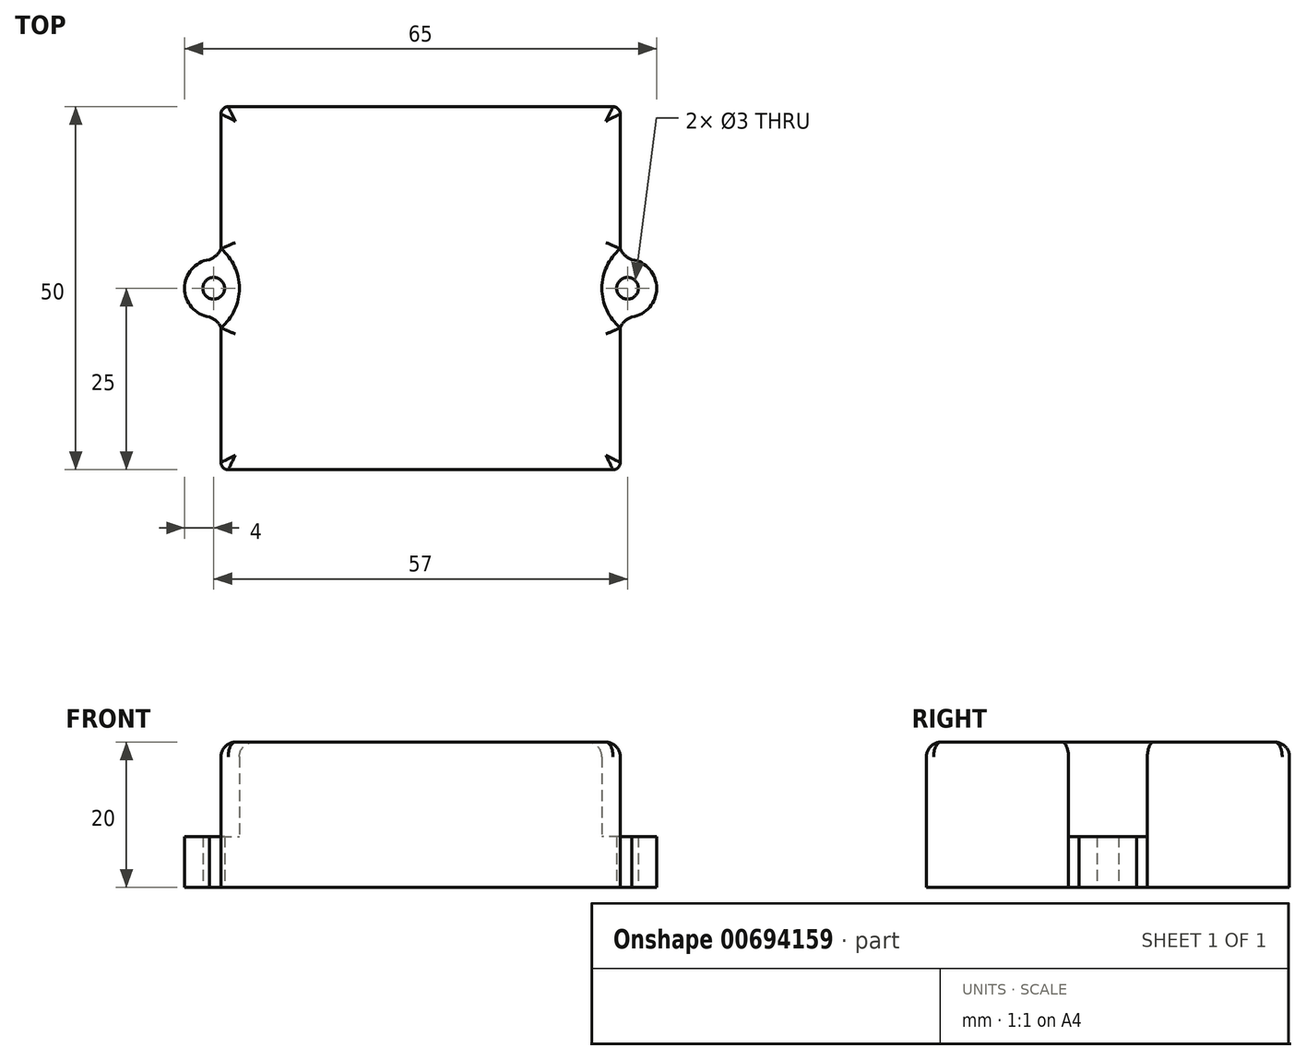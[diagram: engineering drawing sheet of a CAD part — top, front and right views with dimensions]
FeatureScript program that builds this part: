
annotation { "Feature Type Name" : "Feature", "Feature Type Description" : "" }
export const myFeature = defineFeature(function(context is Context, id is Id, definition is map)
    precondition{}
    {
        {
            var Q0;
            Q0=qCreatedBy(makeId("Top.planeOp"),FACE);
            var sketch = newSketch(context, id + "F0", { "sketchPlane" : qUnion([Q0])});
            skLineSegment(sketch, "E0.bottom", {"start": v(-26.5, -25) * mm, "end": v(26.5, -25) * mm});
            skLineSegment(sketch, "E0.top", {"start": v(-26.5, 25) * mm, "end": v(26.5, 25) * mm});
            skLineSegment(sketch, "E0.left", {"start": v(-27.5, -24) * mm, "end": v(-27.5, -5.43) * mm});
            skLineSegment(sketch, "E0.right", {"start": v(27.5, -24) * mm, "end": v(27.5, -5.43) * mm});
            skPoint(sketch, "E0.middle", {"position": v(0, 0) * mm});
            skCircle(sketch, "E1", {"center": v(-28.5, 0) * mm, "radius": 1.5 * mm});
            skCircle(sketch, "E2", {"center": v(28.5, 0) * mm, "radius": 1.5 * mm});
            skPoint(sketch, "E3", {"position": v(-27.5, 0) * mm});
            skArc(sketch, "E4", {"start": v(-29.11, 3.95) * mm, "mid": v(-32.5, 0) * mm, "end": v(-29.11, -3.95) * mm});
            skArc(sketch, "E5", {"start": v(29.11, -3.95) * mm, "mid": v(32.5, 0) * mm, "end": v(29.11, 3.95) * mm});
            skArc(sketch, "E6", {"start": v(-29.11, 3.95) * mm, "mid": v(-28.15, 4.52) * mm, "end": v(-27.5, 5.43) * mm});
            skArc(sketch, "E7.MirrorCS", {"start": v(-29.11, -3.95) * mm, "mid": v(-28.15, -4.52) * mm, "end": v(-27.5, -5.43) * mm});
            skArc(sketch, "E8.MirrorCS", {"start": v(29.11, 3.95) * mm, "mid": v(28.15, 4.52) * mm, "end": v(27.5, 5.43) * mm});
            skArc(sketch, "E9.MirrorCS", {"start": v(29.11, -3.95) * mm, "mid": v(28.15, -4.52) * mm, "end": v(27.5, -5.43) * mm});
            skLineSegment(sketch, "E10.trimOffspring", {"start": v(-27.5, 5.43) * mm, "end": v(-27.5, 24) * mm});
            skLineSegment(sketch, "E11.trimOffspring", {"start": v(27.5, 5.43) * mm, "end": v(27.5, 24) * mm});
            skPoint(sketch, "E12.visualSharp", {"position": v(-27.5, 25) * mm});
            skArc(sketch, "E12.filletArc", {"start": v(-26.5, 25) * mm, "mid": v(-27.2, 24.7) * mm, "end": v(-27.5, 24) * mm});
            skPoint(sketch, "E13.visualSharp", {"position": v(-27.5, -25) * mm});
            skArc(sketch, "E13.filletArc", {"start": v(-27.5, -24) * mm, "mid": v(-27.2, -24.7) * mm, "end": v(-26.5, -25) * mm});
            skPoint(sketch, "E14.visualSharp", {"position": v(27.5, -25) * mm});
            skArc(sketch, "E14.filletArc", {"start": v(26.5, -25) * mm, "mid": v(27.2, -24.7) * mm, "end": v(27.5, -24) * mm});
            skPoint(sketch, "E15.visualSharp", {"position": v(27.5, 25) * mm});
            skArc(sketch, "E15.filletArc", {"start": v(27.5, 24) * mm, "mid": v(27.2, 24.7) * mm, "end": v(26.5, 25) * mm});
            skSolve(sketch);
        }
        {
            var Q0;
            Q0 = qSketchRegion(id + "F0", true);
            extrude(context, id + "F1", {"entities" : qUnion([Q0]), "depth" : 7 * mm, "offsetDistance" : 25 * mm});
        }
        {
            var Q0;
            Q0=makeQuery(id+"F1.opExtrude","CAP_FACE",FACE,{"disambiguationData":[OSD([sQuery(id+"F0.wireOp",EDGE,"E0.bottom"),sQuery(id+"F0.wireOp",EDGE,"E0.top"),sQuery(id+"F0.wireOp",EDGE,"E0.left"),sQuery(id+"F0.wireOp",EDGE,"E0.right"),sQuery(id+"F0.wireOp",EDGE,"E1"),sQuery(id+"F0.wireOp",EDGE,"E2"),sQuery(id+"F0.wireOp",EDGE,"E4"),sQuery(id+"F0.wireOp",EDGE,"E5"),sQuery(id+"F0.wireOp",EDGE,"E6"),sQuery(id+"F0.wireOp",EDGE,"E7.MirrorCS"),sQuery(id+"F0.wireOp",EDGE,"E8.MirrorCS"),sQuery(id+"F0.wireOp",EDGE,"E9.MirrorCS"),sQuery(id+"F0.wireOp",EDGE,"E10.trimOffspring"),sQuery(id+"F0.wireOp",EDGE,"E11.trimOffspring"),sQuery(id+"F0.wireOp",EDGE,"E12.filletArc"),sQuery(id+"F0.wireOp",EDGE,"E13.filletArc"),sQuery(id+"F0.wireOp",EDGE,"E14.filletArc"),sQuery(id+"F0.wireOp",EDGE,"E15.filletArc")])],"isStart":false});
            var sketch = newSketch(context, id + "F2", { "sketchPlane" : qUnion([Q0])});
            skLineSegment(sketch, "E16.0.0", {"start": v(26.5, 25) * mm, "end": v(-26.5, 25) * mm});
            skArc(sketch, "E16.0.1", {"start": v(-26.5, 25) * mm, "mid": v(-27.2, 24.7) * mm, "end": v(-27.5, 24) * mm});
            skLineSegment(sketch, "E16.0.2", {"start": v(-27.5, 24) * mm, "end": v(-27.5, 5.43) * mm});
            skArc(sketch, "E16.0.3", {"start": v(-27.5, 5.43) * mm, "mid": v(-28.15, 4.52) * mm, "end": v(-29.11, 3.95) * mm});
            skArc(sketch, "E16.0.4", {"start": v(-29.11, 3.95) * mm, "mid": v(-32.5, 0) * mm, "end": v(-29.11, -3.95) * mm});
            skArc(sketch, "E16.0.5", {"start": v(-29.11, -3.95) * mm, "mid": v(-28.15, -4.52) * mm, "end": v(-27.5, -5.43) * mm});
            skLineSegment(sketch, "E16.0.6", {"start": v(-27.5, -5.43) * mm, "end": v(-27.5, -24) * mm});
            skArc(sketch, "E16.0.7", {"start": v(-27.5, -24) * mm, "mid": v(-27.2, -24.7) * mm, "end": v(-26.5, -25) * mm});
            skLineSegment(sketch, "E16.0.8", {"start": v(-26.5, -25) * mm, "end": v(26.5, -25) * mm});
            skArc(sketch, "E16.0.9", {"start": v(26.5, -25) * mm, "mid": v(27.2, -24.7) * mm, "end": v(27.5, -24) * mm});
            skLineSegment(sketch, "E16.0.10", {"start": v(27.5, -24) * mm, "end": v(27.5, -5.43) * mm});
            skArc(sketch, "E16.0.11", {"start": v(27.5, -5.43) * mm, "mid": v(28.15, -4.52) * mm, "end": v(29.11, -3.95) * mm});
            skArc(sketch, "E16.0.12", {"start": v(29.11, -3.95) * mm, "mid": v(32.5, 0) * mm, "end": v(29.11, 3.95) * mm});
            skArc(sketch, "E16.0.13", {"start": v(29.11, 3.95) * mm, "mid": v(28.15, 4.52) * mm, "end": v(27.5, 5.43) * mm});
            skLineSegment(sketch, "E16.0.14", {"start": v(27.5, 5.43) * mm, "end": v(27.5, 24) * mm});
            skArc(sketch, "E16.0.15", {"start": v(27.5, 24) * mm, "mid": v(27.2, 24.7) * mm, "end": v(26.5, 25) * mm});
            skArc(sketch, "E17", {"start": v(-27.5, -5.43) * mm, "mid": v(-24.96, 0) * mm, "end": v(-27.5, 5.43) * mm});
            skPoint(sketch, "E17.third.point", {"position": v(-25.02, 0.9) * mm});
            skArc(sketch, "E18.MirrorC", {"start": v(27.5, -5.43) * mm, "mid": v(24.96, 0) * mm, "end": v(27.5, 5.43) * mm});
            skSolve(sketch);
        }
        {
            var Q0;
            Q0=makeQuery(id+"F2.imprint","IMPRINT",FACE,{"disambiguationData":[TD([[makeQuery(id+"F2.imprint","IMPRINT",EDGE,{"derivedFrom":sQuery(id+"F2.wireOp",EDGE,"E16.0.0")}),-1.0]])]});
            extrude(context, id + "F3", {"entities" : qUnion([Q0]), "operationType" : NewBodyOperationType.ADD, "depth" : 13 * mm, "offsetDistance" : 25 * mm});
        }
        {
            var Q0;
            Q0=makeQuery(id+"F3.opExtrude","CAP_FACE",FACE,{"disambiguationData":[OSD([sQuery(id+"F2.wireOp",EDGE,"E16.0.0"),sQuery(id+"F2.wireOp",EDGE,"E16.0.1"),sQuery(id+"F2.wireOp",EDGE,"E16.0.2"),sQuery(id+"F2.wireOp",EDGE,"E16.0.6"),sQuery(id+"F2.wireOp",EDGE,"E16.0.7"),sQuery(id+"F2.wireOp",EDGE,"E16.0.8"),sQuery(id+"F2.wireOp",EDGE,"E16.0.9"),sQuery(id+"F2.wireOp",EDGE,"E16.0.10"),sQuery(id+"F2.wireOp",EDGE,"E16.0.14"),sQuery(id+"F2.wireOp",EDGE,"E16.0.15"),sQuery(id+"F2.wireOp",EDGE,"E17"),sQuery(id+"F2.wireOp",EDGE,"E18.MirrorC")])],"isStart":false});
            fillet(context, id + "F4", {"entities" : qUnion([Q0]), "radius" : 2 * mm, "tangentPropagation" : true, "allowEdgeOverflow" : false});
        }
    });
